# Revit family: Shower-Shower_Column_Kit-KOHLER-JULY-K-99742T_1
name_source: partatom
category: Plumbing Fixtures
units: mm (PartAtom-declared; Revit-internal decimal feet)

## family parameters
Cut with Voids When Loaded = No
Host = Face
OmniClass Number = 23.31.17.00
OmniClass Title = Showers
Part Type = Normal
Room Calculation Point = No
Round Connector Dimension = Use Diameter
Shared = No

## types (2) — shared parameters
ADA Compliant = No
Assembly Code = D2010700
CW Connection = Yes
Cold Water Inlet = Cold Water Inlet
Date Modified = 04/07/2023
Default Elevation = 42"
Drain Included = No
Finish = Kohler-Metal-CP-Polished_Chrome
Flow Rate = 3 GPM
HW Connection = Yes
Height = 50 1/2"
Hot Water Inlet = Hot Water Inlet
Length = 22 3/4"
Manufacturer = Kohler Co.
Master Format 2014 = 22 42 23
Master Format 2014 Name = Residential Showers
Material = Premium Metal Construction
Pressure = 80.00 psi
Product Name = JULY
Spout Reach = 6 11/16"
URL = https://www.kohler.com.cn
Vent Connection = No
Waste Connection = No
Waste Water Outlet = Waste Water Outlet
WaterSense Certified = No
Width = 11 1/8"

## per-type parameters (varying)
| type | Description | Model | Product Documentation Link | Product Page URL | Type |
| C9, CP-Polished Chrome | Qi Yue three outlet shower column (hard pipe connection) | K-99742T-C9-CP | https://files.kohler.com.cn | https://www.kohler.com.cn | 1 |
| C9E2, CP-Polished Chrome | 3 WAY SHOWER COLUMN | K-99742T-C9E2-CP |  |  | 2 |

## geometry (parser evidence)
native form markers: Sweep x4
no freeform markers — native parametric forms only
